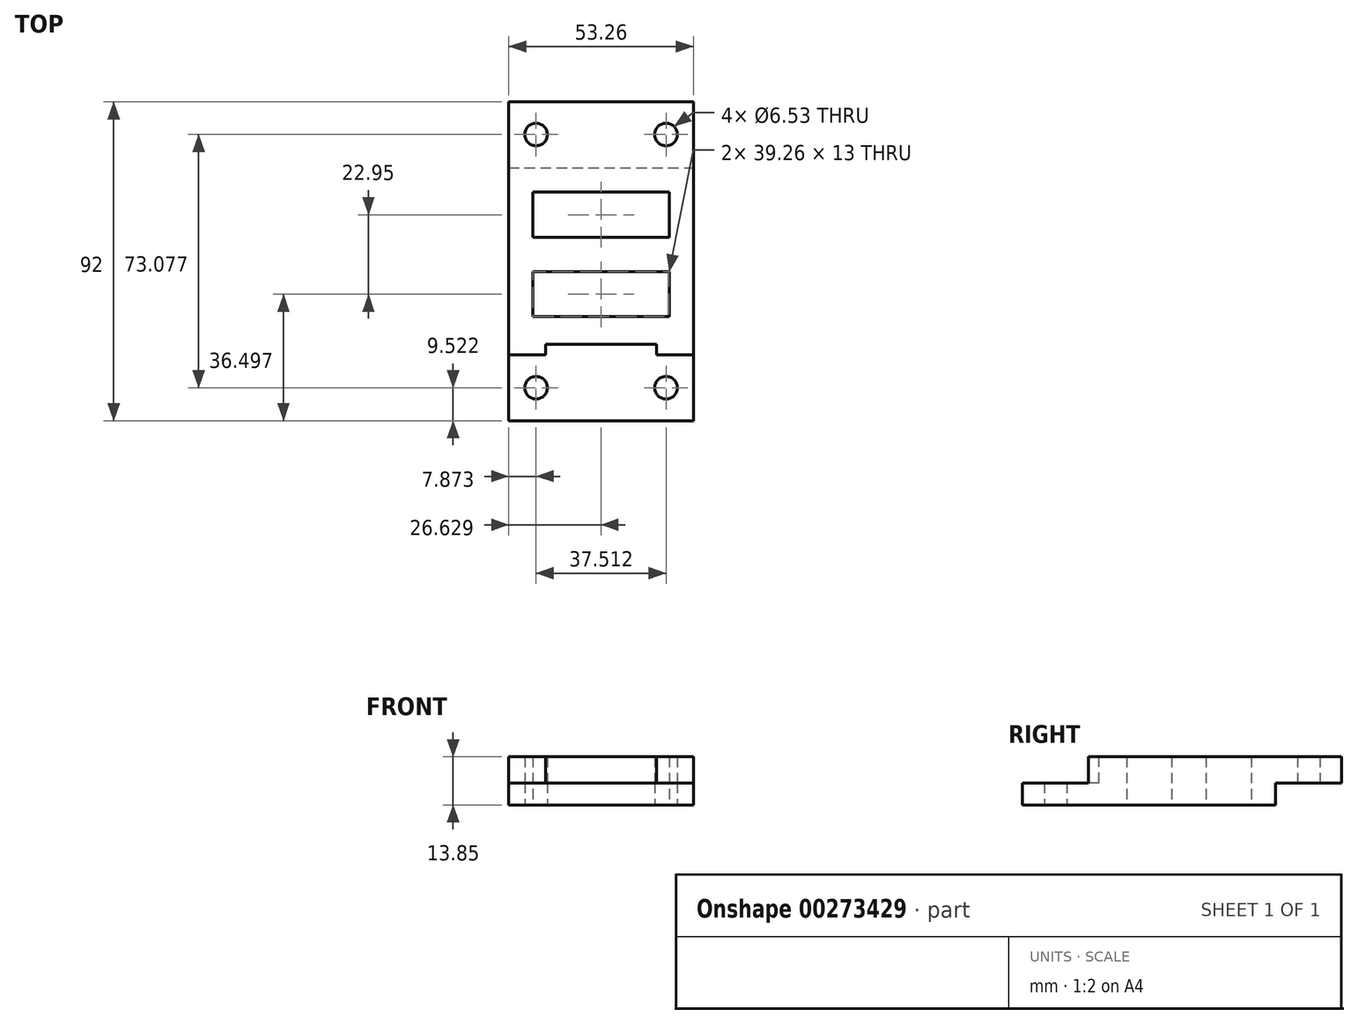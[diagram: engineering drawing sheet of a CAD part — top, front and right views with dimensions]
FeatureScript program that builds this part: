
annotation { "Feature Type Name" : "Feature", "Feature Type Description" : "" }
export const myFeature = defineFeature(function(context is Context, id is Id, definition is map)
    precondition{}
    {
        {
            var Q0;
            Q0=qCreatedBy(makeId("Top.planeOp"),FACE);
            var sketch = newSketch(context, id + "F0", { "sketchPlane" : qUnion([Q0])});
            skLineSegment(sketch, "E0.bottom", {"start": v(-22.71, 51.04) * mm, "end": v(30.55, 51.04) * mm});
            skLineSegment(sketch, "E0.top", {"start": v(-22.71, -40.96) * mm, "end": v(30.55, -40.96) * mm});
            skLineSegment(sketch, "E0.left", {"start": v(-22.71, 51.04) * mm, "end": v(-22.71, -40.96) * mm});
            skLineSegment(sketch, "E0.right", {"start": v(30.55, 51.04) * mm, "end": v(30.55, -40.96) * mm});
            skPoint(sketch, "E1", {"position": v(-14.84, -31.44) * mm});
            skPoint(sketch, "E2", {"position": v(22.68, -31.44) * mm});
            skPoint(sketch, "E3", {"position": v(-14.84, 41.64) * mm});
            skPoint(sketch, "E4", {"position": v(22.68, 41.64) * mm});
            skSolve(sketch);
        }
        {
            var Q0;
            Q0=makeQuery(id+"F0.imprint","IMPRINT",FACE,{"disambiguationData":[TD([[makeQuery(id+"F0.imprint","IMPRINT",EDGE,{"derivedFrom":sQuery(id+"F0.wireOp",EDGE,"E0.bottom")}),-1.0]])]});
            extrude(context, id + "F1", {"entities" : qUnion([Q0]), "depth" : 12.7 * mm});
        }
        {
            var Q0;
            Q0=makeQuery(id+"F1.opExtrude","CAP_FACE",FACE,{"disambiguationData":[OSD([sQuery(id+"F0.wireOp",EDGE,"E0.bottom"),sQuery(id+"F0.wireOp",EDGE,"E0.top"),sQuery(id+"F0.wireOp",EDGE,"E0.left"),sQuery(id+"F0.wireOp",EDGE,"E0.right")])],"isStart":true});
            var sketch = newSketch(context, id + "F2", { "sketchPlane" : qUnion([Q0])});
            skLineSegment(sketch, "E5.bottom", {"start": v(-22.71, -51.04) * mm, "end": v(30.55, -51.04) * mm});
            skLineSegment(sketch, "E5.top", {"start": v(-22.71, -31.99) * mm, "end": v(30.55, -31.99) * mm});
            skLineSegment(sketch, "E5.left", {"start": v(-22.71, -51.04) * mm, "end": v(-22.71, -31.99) * mm});
            skLineSegment(sketch, "E5.right", {"start": v(30.55, -51.04) * mm, "end": v(30.55, -31.99) * mm});
            skSolve(sketch);
        }
        {
            var Q0;
            Q0=makeQuery(id+"F2.imprint","IMPRINT",FACE,{"disambiguationData":[TD([[makeQuery(id+"F2.imprint","IMPRINT",EDGE,{"derivedFrom":sQuery(id+"F2.wireOp",EDGE,"E5.bottom")}),1.0]])]});
            extrude(context, id + "F3", {"entities" : qUnion([Q0]), "operationType" : NewBodyOperationType.REMOVE, "oppositeDirection" : true, "depth" : 6.35 * mm});
        }
        {
            var Q0;
            Q0=makeQuery(id+"F1.opExtrude","CAP_FACE",FACE,{"disambiguationData":[OSD([sQuery(id+"F0.wireOp",EDGE,"E0.bottom"),sQuery(id+"F0.wireOp",EDGE,"E0.top"),sQuery(id+"F0.wireOp",EDGE,"E0.left"),sQuery(id+"F0.wireOp",EDGE,"E0.right")])],"isStart":false});
            var sketch = newSketch(context, id + "F4", { "sketchPlane" : qUnion([Q0])});
            skLineSegment(sketch, "E6.bottom", {"start": v(-22.71, -40.96) * mm, "end": v(30.55, -40.96) * mm});
            skLineSegment(sketch, "E6.top", {"start": v(-22.71, -21.91) * mm, "end": v(30.55, -21.91) * mm});
            skLineSegment(sketch, "E6.left", {"start": v(-22.71, -40.96) * mm, "end": v(-22.71, -21.91) * mm});
            skLineSegment(sketch, "E6.right", {"start": v(30.55, -40.96) * mm, "end": v(30.55, -21.91) * mm});
            skSolve(sketch);
        }
        {
            var Q0;
            Q0=makeQuery(id+"F4.imprint","IMPRINT",FACE,{"disambiguationData":[TD([[makeQuery(id+"F4.imprint","IMPRINT",EDGE,{"derivedFrom":sQuery(id+"F4.wireOp",EDGE,"E6.bottom")}),1.0]])]});
            extrude(context, id + "F5", {"entities" : qUnion([Q0]), "operationType" : NewBodyOperationType.REMOVE, "oppositeDirection" : true, "depth" : 6.35 * mm});
        }
        {
            var Q0;
            Q0=makeQuery(id+"F1.opExtrude","CAP_FACE",FACE,{"disambiguationData":[OSD([sQuery(id+"F0.wireOp",EDGE,"E0.bottom"),sQuery(id+"F0.wireOp",EDGE,"E0.top"),sQuery(id+"F0.wireOp",EDGE,"E0.left"),sQuery(id+"F0.wireOp",EDGE,"E0.right")])],"isStart":false});
            extrude(context, id + "F6", {"entities" : qUnion([Q0]), "operationType" : NewBodyOperationType.ADD, "depth" : 1.15 * mm});
        }
        {
            var Q0;
            Q0=sQuery(id+"F0.wireOp",VERTEX,"E1");
            var Q1;
            Q1=sQuery(id+"F0.wireOp",VERTEX,"E2");
            var Q2;
            Q2=sQuery(id+"F0.wireOp",VERTEX,"E3");
            var Q3;
            Q3=sQuery(id+"F0.wireOp",VERTEX,"E4");
            var Q4;
            Q4=makeQuery(id+"F1.opExtrude","SWEPT_BODY",BODY,{"disambiguationData":[OSD([sQuery(id+"F0.wireOp",EDGE,"E0.bottom"),sQuery(id+"F0.wireOp",EDGE,"E0.top"),sQuery(id+"F0.wireOp",EDGE,"E0.left"),sQuery(id+"F0.wireOp",EDGE,"E0.right")])]});
            hole(context, id + "F7", {"style" : HoleStyle.SIMPLE, "endStyle" : HoleEndStyle.THROUGH, "oppositeDirection" : true, "holeDiameter" : 6.53 * mm, "tappedDepth" : 12 * mm, "tapClearance" : 3, "locations" : qUnion([Q0, Q1, Q2, Q3]), "scope" : qUnion([Q4])});
        }
        {
            var Q0;
            Q0=makeQuery(id+"F1.opExtrude","CAP_FACE",FACE,{"disambiguationData":[OSD([sQuery(id+"F0.wireOp",EDGE,"E0.bottom"),sQuery(id+"F0.wireOp",EDGE,"E0.top"),sQuery(id+"F0.wireOp",EDGE,"E0.left"),sQuery(id+"F0.wireOp",EDGE,"E0.right")])],"isStart":true});
            var sketch = newSketch(context, id + "F8", { "sketchPlane" : qUnion([Q0])});
            skLineSegment(sketch, "E7.bottom", {"start": v(-15.71, 10.96) * mm, "end": v(23.55, 10.96) * mm});
            skLineSegment(sketch, "E7.top", {"start": v(-15.71, -2.04) * mm, "end": v(23.55, -2.04) * mm});
            skLineSegment(sketch, "E7.left", {"start": v(-15.71, 10.96) * mm, "end": v(-15.71, -2.04) * mm});
            skLineSegment(sketch, "E7.right", {"start": v(23.55, 10.96) * mm, "end": v(23.55, -2.04) * mm});
            skLineSegment(sketch, "E8.bottom", {"start": v(-15.71, -11.99) * mm, "end": v(23.55, -11.99) * mm});
            skLineSegment(sketch, "E8.top", {"start": v(-15.71, -24.99) * mm, "end": v(23.55, -24.99) * mm});
            skLineSegment(sketch, "E8.left", {"start": v(-15.71, -11.99) * mm, "end": v(-15.71, -24.99) * mm});
            skLineSegment(sketch, "E8.right", {"start": v(23.55, -11.99) * mm, "end": v(23.55, -24.99) * mm});
            skSolve(sketch);
        }
        {
            var Q0;
            Q0=makeQuery(id+"F8.imprint","IMPRINT",FACE,{"disambiguationData":[TD([[makeQuery(id+"F8.imprint","IMPRINT",EDGE,{"derivedFrom":sQuery(id+"F8.wireOp",EDGE,"E7.bottom")}),-1.0]])]});
            var Q1;
            Q1=makeQuery(id+"F8.imprint","IMPRINT",FACE,{"disambiguationData":[TD([[makeQuery(id+"F8.imprint","IMPRINT",EDGE,{"derivedFrom":sQuery(id+"F8.wireOp",EDGE,"E8.bottom")}),-1.0]])]});
            extrude(context, id + "F9", {"entities" : qUnion([Q0, Q1]), "operationType" : NewBodyOperationType.REMOVE, "endBound" : BoundingType.THROUGH_ALL, "oppositeDirection" : true, "depth" : 25 * mm});
        }
        {
            var Q0;
            {var subQ0=sQuery(id+"F4.wireOp",EDGE,"E6.top");Q0=makeQuery(id+"F6.boolean.opBoolean","MERGE",FACE,{"derivedFrom":[makeQuery(id+"F5.boolean.opBoolean","COPY",FACE,{"derivedFrom":makeQuery(id+"F5.opExtrude","SWEPT_FACE",FACE,{"disambiguationData":[OSD([subQ0])]})}),makeQuery(id+"F6.opExtrude","SWEPT_FACE",FACE,{"disambiguationData":[OSD([subQ0])]})]});}
            var sketch = newSketch(context, id + "F10", { "sketchPlane" : qUnion([Q0])});
            skLineSegment(sketch, "E9.bottom", {"start": v(19.92, 6.35) * mm, "end": v(-12.08, 6.35) * mm});
            skLineSegment(sketch, "E9.top", {"start": v(19.92, 13.85) * mm, "end": v(-12.08, 13.85) * mm});
            skLineSegment(sketch, "E9.left", {"start": v(19.92, 6.35) * mm, "end": v(19.92, 13.85) * mm});
            skLineSegment(sketch, "E9.right", {"start": v(-12.08, 6.35) * mm, "end": v(-12.08, 13.85) * mm});
            skSolve(sketch);
        }
        {
            var Q0;
            Q0=makeQuery(id+"F10.imprint","IMPRINT",FACE,{"disambiguationData":[TD([[makeQuery(id+"F10.imprint","IMPRINT",EDGE,{"derivedFrom":sQuery(id+"F10.wireOp",EDGE,"E9.bottom")}),1.0]])]});
            extrude(context, id + "F11", {"entities" : qUnion([Q0]), "operationType" : NewBodyOperationType.REMOVE, "oppositeDirection" : true, "depth" : 3 * mm});
        }
    });
